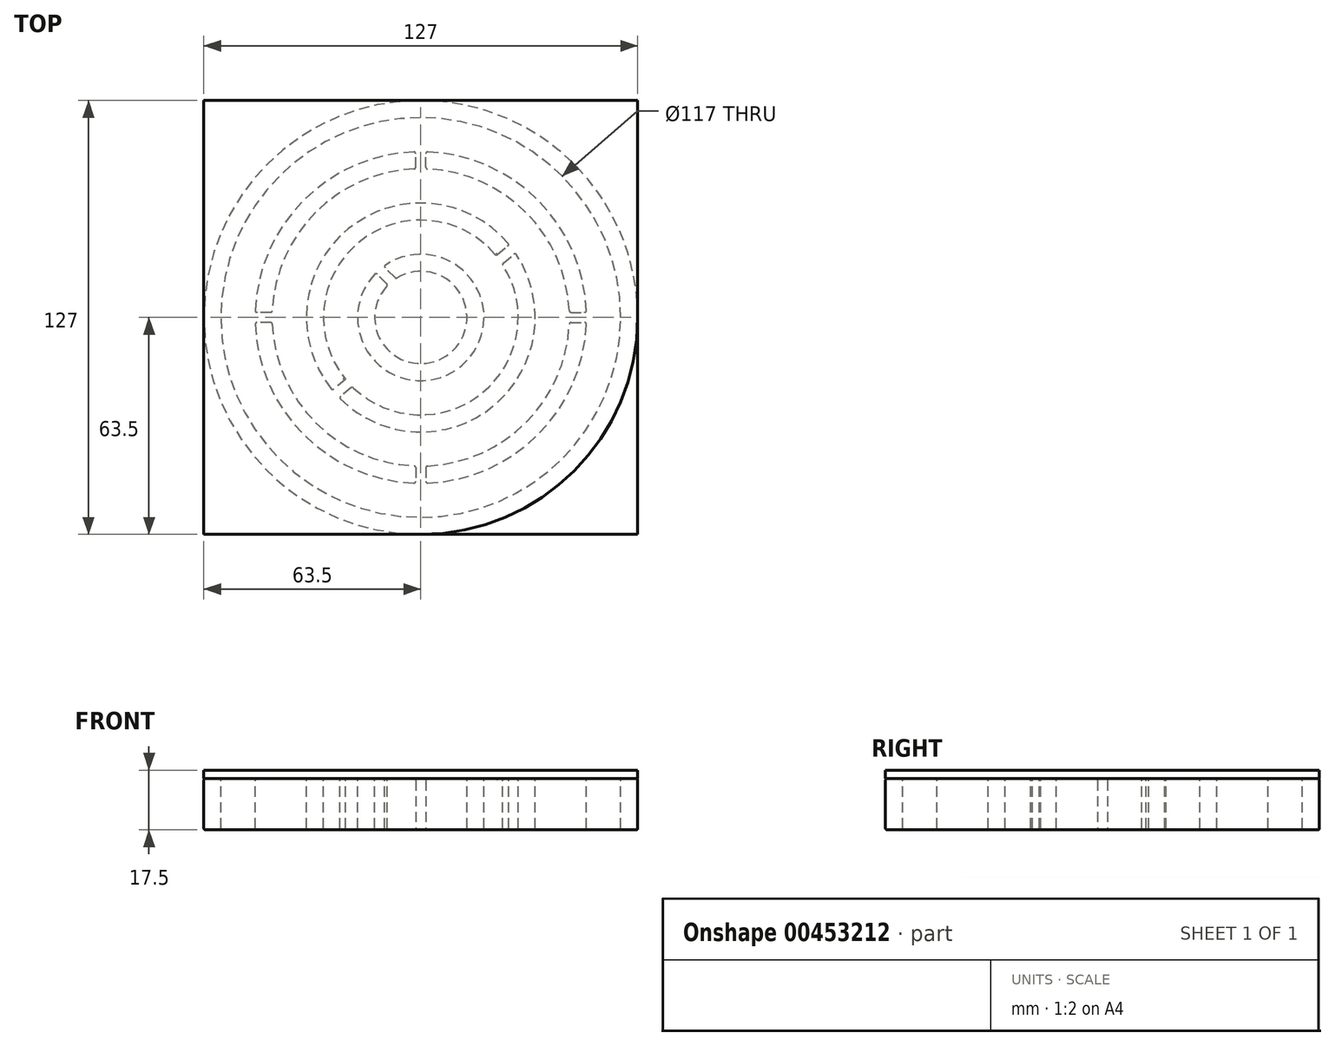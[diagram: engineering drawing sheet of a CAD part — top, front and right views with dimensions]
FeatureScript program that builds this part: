
annotation { "Feature Type Name" : "Feature", "Feature Type Description" : "" }
export const myFeature = defineFeature(function(context is Context, id is Id, definition is map)
    precondition{}
    {
        {
            var Q0;
            Q0=qCreatedBy(makeId("Top.planeOp"),FACE);
            var sketch = newSketch(context, id + "F0", { "sketchPlane" : qUnion([Q0])});
            skCircle(sketch, "E0", {"center": v(0, 0) * mm, "radius": 63.5 * mm});
            skCircle(sketch, "E1", {"center": v(0, 0) * mm, "radius": 58.5 * mm});
            skCircle(sketch, "E2", {"center": v(0, 0) * mm, "radius": 48.5 * mm});
            skCircle(sketch, "E3", {"center": v(0, 0) * mm, "radius": 43.5 * mm});
            skLineSegment(sketch, "E4", {"start": v(0, 0) * mm, "end": v(0, 48.5) * mm});
            skLineSegment(sketch, "E5", {"start": v(0, 0) * mm, "end": v(0, -48.5) * mm});
            skLineSegment(sketch, "E6", {"start": v(0, 0) * mm, "end": v(48.5, 0) * mm});
            skLineSegment(sketch, "E7", {"start": v(0, 0) * mm, "end": v(-48.5, 0) * mm});
            skLineSegment(sketch, "E8.0", {"start": v(1.5, 0) * mm, "end": v(1.5, 48.5) * mm});
            skLineSegment(sketch, "E9.0", {"start": v(-1.5, 0) * mm, "end": v(-1.5, 48.5) * mm});
            skLineSegment(sketch, "E10.0", {"start": v(-1.5, 0) * mm, "end": v(-1.5, -48.5) * mm});
            skLineSegment(sketch, "E11.0", {"start": v(1.5, 0) * mm, "end": v(1.5, -48.5) * mm});
            skLineSegment(sketch, "E12.0", {"start": v(0, -1.5) * mm, "end": v(48.5, -1.5) * mm});
            skLineSegment(sketch, "E13.0", {"start": v(0, 1.5) * mm, "end": v(48.5, 1.5) * mm});
            skLineSegment(sketch, "E14.0", {"start": v(0, 1.5) * mm, "end": v(-48.5, 1.5) * mm});
            skLineSegment(sketch, "E15.0", {"start": v(0, -1.5) * mm, "end": v(-48.5, -1.5) * mm});
            skCircle(sketch, "E16", {"center": v(0, 0) * mm, "radius": 33.5 * mm});
            skCircle(sketch, "E17", {"center": v(0, 0) * mm, "radius": 28.5 * mm});
            skCircle(sketch, "E18", {"center": v(0, 0) * mm, "radius": 18.5 * mm});
            skCircle(sketch, "E19", {"center": v(0, 0) * mm, "radius": 13.5 * mm});
            skLineSegment(sketch, "E20", {"start": v(0, 0) * mm, "end": v(-13.14, 13.02) * mm});
            skLineSegment(sketch, "E21", {"start": v(0, 0) * mm, "end": v(13.14, -13.02) * mm});
            skLineSegment(sketch, "E22.0", {"start": v(2.11, 2.13) * mm, "end": v(-11.03, 15.15) * mm});
            skLineSegment(sketch, "E23.0", {"start": v(2.11, 2.13) * mm, "end": v(15.25, -10.89) * mm});
            skLineSegment(sketch, "E24", {"start": v(0, 0) * mm, "end": v(-25.9, -21.26) * mm});
            skLineSegment(sketch, "E25", {"start": v(0, 0) * mm, "end": v(25.9, 21.26) * mm});
            skLineSegment(sketch, "E26.0", {"start": v(1.9, -2.32) * mm, "end": v(27.8, 18.94) * mm});
            skLineSegment(sketch, "E27.0", {"start": v(1.9, -2.32) * mm, "end": v(-23.99, -23.57) * mm});
            skSolve(sketch);
        }
        {
            var Q0;
            Q0=makeQuery(id+"F0.imprint","IMPRINT",FACE,{"disambiguationData":[TD([[makeQuery(id+"F0.imprint","IMPRINT",EDGE,{"derivedFrom":sQuery(id+"F0.wireOp",EDGE,"E0")}),1.0]])]});
            var Q1;
            {var subQ0=sQuery(id+"F0.wireOp",EDGE,"E15.0");var subQ1=sQuery(id+"F0.wireOp",EDGE,"E2");var subQ2=makeQuery(id+"F0.imprint","INTERSECT",VERTEX,{"derivedFrom":[subQ1,subQ0]});Q1=makeQuery(id+"F0.imprint","IMPRINT",FACE,{"disambiguationData":[TD([[makeQuery(id+"F0.imprint","IMPRINT",EDGE,{"disambiguationData":[TD([[subQ2,-1.0]])],"derivedFrom":subQ1}),1.0]])]});}
            var Q2;
            {var subQ0=sQuery(id+"F0.wireOp",EDGE,"E9.0");var subQ1=sQuery(id+"F0.wireOp",EDGE,"E2");var subQ2=makeQuery(id+"F0.imprint","INTERSECT",VERTEX,{"derivedFrom":[subQ1,subQ0]});Q2=makeQuery(id+"F0.imprint","IMPRINT",FACE,{"disambiguationData":[TD([[makeQuery(id+"F0.imprint","IMPRINT",EDGE,{"disambiguationData":[TD([[subQ2,-1.0]])],"derivedFrom":subQ1}),1.0]])]});}
            var Q3;
            {var subQ0=sQuery(id+"F0.wireOp",EDGE,"E13.0");var subQ1=sQuery(id+"F0.wireOp",EDGE,"E2");var subQ2=makeQuery(id+"F0.imprint","INTERSECT",VERTEX,{"derivedFrom":[subQ1,subQ0]});Q3=makeQuery(id+"F0.imprint","IMPRINT",FACE,{"disambiguationData":[TD([[makeQuery(id+"F0.imprint","IMPRINT",EDGE,{"disambiguationData":[TD([[subQ2,-1.0]])],"derivedFrom":subQ1}),1.0]])]});}
            var Q4;
            {var subQ0=sQuery(id+"F0.wireOp",EDGE,"E11.0");var subQ1=sQuery(id+"F0.wireOp",EDGE,"E2");var subQ2=makeQuery(id+"F0.imprint","INTERSECT",VERTEX,{"derivedFrom":[subQ1,subQ0]});Q4=makeQuery(id+"F0.imprint","IMPRINT",FACE,{"disambiguationData":[TD([[makeQuery(id+"F0.imprint","IMPRINT",EDGE,{"disambiguationData":[TD([[subQ2,-1.0]])],"derivedFrom":subQ1}),1.0]])]});}
            var Q5;
            {var subQ0=sQuery(id+"F0.wireOp",EDGE,"E17");var subQ1=sQuery(id+"F0.wireOp",EDGE,"E15.0");var subQ2=makeQuery(id+"F0.imprint","INTERSECT",VERTEX,{"derivedFrom":[subQ1,subQ0]});Q5=makeQuery(id+"F0.imprint","IMPRINT",FACE,{"disambiguationData":[TD([[makeQuery(id+"F0.imprint","IMPRINT",EDGE,{"disambiguationData":[TD([[subQ2,-1.0]])],"derivedFrom":subQ1}),1.0]])]});}
            var Q6;
            {var subQ0=sQuery(id+"F0.wireOp",EDGE,"E17");var subQ1=sQuery(id+"F0.wireOp",EDGE,"E7");var subQ2=makeQuery(id+"F0.imprint","INTERSECT",VERTEX,{"derivedFrom":[subQ1,subQ0]});Q6=makeQuery(id+"F0.imprint","IMPRINT",FACE,{"disambiguationData":[TD([[makeQuery(id+"F0.imprint","IMPRINT",EDGE,{"disambiguationData":[TD([[subQ2,-1.0]])],"derivedFrom":subQ1}),1.0]])]});}
            var Q7;
            {var subQ0=sQuery(id+"F0.wireOp",EDGE,"E17");var subQ1=sQuery(id+"F0.wireOp",EDGE,"E7");var subQ2=makeQuery(id+"F0.imprint","INTERSECT",VERTEX,{"derivedFrom":[subQ1,subQ0]});Q7=makeQuery(id+"F0.imprint","IMPRINT",FACE,{"disambiguationData":[TD([[makeQuery(id+"F0.imprint","IMPRINT",EDGE,{"disambiguationData":[TD([[subQ2,-1.0]])],"derivedFrom":subQ1}),-1.0]])]});}
            var Q8;
            {var subQ0=sQuery(id+"F0.wireOp",EDGE,"E17");var subQ1=sQuery(id+"F0.wireOp",EDGE,"E9.0");var subQ2=makeQuery(id+"F0.imprint","INTERSECT",VERTEX,{"derivedFrom":[subQ1,subQ0]});Q8=makeQuery(id+"F0.imprint","IMPRINT",FACE,{"disambiguationData":[TD([[makeQuery(id+"F0.imprint","IMPRINT",EDGE,{"disambiguationData":[TD([[subQ2,-1.0]])],"derivedFrom":subQ1}),1.0]])]});}
            var Q9;
            {var subQ0=sQuery(id+"F0.wireOp",EDGE,"E17");var subQ1=sQuery(id+"F0.wireOp",EDGE,"E4");var subQ2=makeQuery(id+"F0.imprint","INTERSECT",VERTEX,{"derivedFrom":[subQ1,subQ0]});Q9=makeQuery(id+"F0.imprint","IMPRINT",FACE,{"disambiguationData":[TD([[makeQuery(id+"F0.imprint","IMPRINT",EDGE,{"disambiguationData":[TD([[subQ2,-1.0]])],"derivedFrom":subQ1}),1.0]])]});}
            var Q10;
            {var subQ0=sQuery(id+"F0.wireOp",EDGE,"E17");var subQ1=sQuery(id+"F0.wireOp",EDGE,"E4");var subQ2=makeQuery(id+"F0.imprint","INTERSECT",VERTEX,{"derivedFrom":[subQ1,subQ0]});Q10=makeQuery(id+"F0.imprint","IMPRINT",FACE,{"disambiguationData":[TD([[makeQuery(id+"F0.imprint","IMPRINT",EDGE,{"disambiguationData":[TD([[subQ2,-1.0]])],"derivedFrom":subQ1}),-1.0]])]});}
            var Q11;
            {var subQ0=sQuery(id+"F0.wireOp",EDGE,"E17");var subQ1=sQuery(id+"F0.wireOp",EDGE,"E8.0");var subQ2=makeQuery(id+"F0.imprint","INTERSECT",VERTEX,{"derivedFrom":[subQ1,subQ0]});Q11=makeQuery(id+"F0.imprint","IMPRINT",FACE,{"disambiguationData":[TD([[makeQuery(id+"F0.imprint","IMPRINT",EDGE,{"disambiguationData":[TD([[subQ2,-1.0]])],"derivedFrom":subQ1}),-1.0]])]});}
            var Q12;
            {var subQ0=sQuery(id+"F0.wireOp",EDGE,"E17");var subQ1=sQuery(id+"F0.wireOp",EDGE,"E13.0");var subQ2=makeQuery(id+"F0.imprint","INTERSECT",VERTEX,{"derivedFrom":[subQ1,subQ0]});Q12=makeQuery(id+"F0.imprint","IMPRINT",FACE,{"disambiguationData":[TD([[makeQuery(id+"F0.imprint","IMPRINT",EDGE,{"disambiguationData":[TD([[subQ2,-1.0]])],"derivedFrom":subQ1}),1.0]])]});}
            var Q13;
            {var subQ0=sQuery(id+"F0.wireOp",EDGE,"E17");var subQ1=sQuery(id+"F0.wireOp",EDGE,"E6");var subQ2=makeQuery(id+"F0.imprint","INTERSECT",VERTEX,{"derivedFrom":[subQ1,subQ0]});Q13=makeQuery(id+"F0.imprint","IMPRINT",FACE,{"disambiguationData":[TD([[makeQuery(id+"F0.imprint","IMPRINT",EDGE,{"disambiguationData":[TD([[subQ2,-1.0]])],"derivedFrom":subQ1}),1.0]])]});}
            var Q14;
            {var subQ0=sQuery(id+"F0.wireOp",EDGE,"E17");var subQ1=sQuery(id+"F0.wireOp",EDGE,"E6");var subQ2=makeQuery(id+"F0.imprint","INTERSECT",VERTEX,{"derivedFrom":[subQ1,subQ0]});Q14=makeQuery(id+"F0.imprint","IMPRINT",FACE,{"disambiguationData":[TD([[makeQuery(id+"F0.imprint","IMPRINT",EDGE,{"disambiguationData":[TD([[subQ2,-1.0]])],"derivedFrom":subQ1}),-1.0]])]});}
            var Q15;
            {var subQ0=sQuery(id+"F0.wireOp",EDGE,"E17");var subQ1=sQuery(id+"F0.wireOp",EDGE,"E11.0");var subQ2=makeQuery(id+"F0.imprint","INTERSECT",VERTEX,{"derivedFrom":[subQ1,subQ0]});Q15=makeQuery(id+"F0.imprint","IMPRINT",FACE,{"disambiguationData":[TD([[makeQuery(id+"F0.imprint","IMPRINT",EDGE,{"disambiguationData":[TD([[subQ2,-1.0]])],"derivedFrom":subQ1}),1.0]])]});}
            var Q16;
            {var subQ0=sQuery(id+"F0.wireOp",EDGE,"E17");var subQ1=sQuery(id+"F0.wireOp",EDGE,"E5");var subQ2=makeQuery(id+"F0.imprint","INTERSECT",VERTEX,{"derivedFrom":[subQ1,subQ0]});Q16=makeQuery(id+"F0.imprint","IMPRINT",FACE,{"disambiguationData":[TD([[makeQuery(id+"F0.imprint","IMPRINT",EDGE,{"disambiguationData":[TD([[subQ2,-1.0]])],"derivedFrom":subQ1}),1.0]])]});}
            var Q17;
            {var subQ0=sQuery(id+"F0.wireOp",EDGE,"E17");var subQ1=sQuery(id+"F0.wireOp",EDGE,"E5");var subQ2=makeQuery(id+"F0.imprint","INTERSECT",VERTEX,{"derivedFrom":[subQ1,subQ0]});Q17=makeQuery(id+"F0.imprint","IMPRINT",FACE,{"disambiguationData":[TD([[makeQuery(id+"F0.imprint","IMPRINT",EDGE,{"disambiguationData":[TD([[subQ2,-1.0]])],"derivedFrom":subQ1}),-1.0]])]});}
            var Q18;
            {var subQ0=sQuery(id+"F0.wireOp",EDGE,"E17");var subQ1=sQuery(id+"F0.wireOp",EDGE,"E10.0");var subQ2=makeQuery(id+"F0.imprint","INTERSECT",VERTEX,{"derivedFrom":[subQ1,subQ0]});Q18=makeQuery(id+"F0.imprint","IMPRINT",FACE,{"disambiguationData":[TD([[makeQuery(id+"F0.imprint","IMPRINT",EDGE,{"disambiguationData":[TD([[subQ2,-1.0]])],"derivedFrom":subQ1}),-1.0]])]});}
            var Q19;
            {var subQ0=sQuery(id+"F0.wireOp",EDGE,"E19");var subQ1=sQuery(id+"F0.wireOp",EDGE,"E15.0");var subQ2=makeQuery(id+"F0.imprint","INTERSECT",VERTEX,{"derivedFrom":[subQ1,subQ0]});Q19=makeQuery(id+"F0.imprint","IMPRINT",FACE,{"disambiguationData":[TD([[makeQuery(id+"F0.imprint","IMPRINT",EDGE,{"disambiguationData":[TD([[subQ2,-1.0]])],"derivedFrom":subQ1}),1.0]])]});}
            var Q20;
            {var subQ0=sQuery(id+"F0.wireOp",EDGE,"E24");var subQ1=sQuery(id+"F0.wireOp",EDGE,"E18");var subQ2=makeQuery(id+"F0.imprint","INTERSECT",VERTEX,{"derivedFrom":[subQ1,subQ0]});Q20=makeQuery(id+"F0.imprint","IMPRINT",FACE,{"disambiguationData":[TD([[makeQuery(id+"F0.imprint","IMPRINT",EDGE,{"disambiguationData":[TD([[subQ2,-1.0]])],"derivedFrom":subQ1}),1.0]])]});}
            var Q21;
            {var subQ0=sQuery(id+"F0.wireOp",EDGE,"E19");var subQ1=sQuery(id+"F0.wireOp",EDGE,"E10.0");var subQ2=makeQuery(id+"F0.imprint","INTERSECT",VERTEX,{"derivedFrom":[subQ1,subQ0]});Q21=makeQuery(id+"F0.imprint","IMPRINT",FACE,{"disambiguationData":[TD([[makeQuery(id+"F0.imprint","IMPRINT",EDGE,{"disambiguationData":[TD([[subQ2,-1.0]])],"derivedFrom":subQ1}),-1.0]])]});}
            var Q22;
            {var subQ0=sQuery(id+"F0.wireOp",EDGE,"E19");var subQ1=sQuery(id+"F0.wireOp",EDGE,"E5");var subQ2=makeQuery(id+"F0.imprint","INTERSECT",VERTEX,{"derivedFrom":[subQ1,subQ0]});Q22=makeQuery(id+"F0.imprint","IMPRINT",FACE,{"disambiguationData":[TD([[makeQuery(id+"F0.imprint","IMPRINT",EDGE,{"disambiguationData":[TD([[subQ2,-1.0]])],"derivedFrom":subQ1}),-1.0]])]});}
            var Q23;
            {var subQ0=sQuery(id+"F0.wireOp",EDGE,"E19");var subQ1=sQuery(id+"F0.wireOp",EDGE,"E5");var subQ2=makeQuery(id+"F0.imprint","INTERSECT",VERTEX,{"derivedFrom":[subQ1,subQ0]});Q23=makeQuery(id+"F0.imprint","IMPRINT",FACE,{"disambiguationData":[TD([[makeQuery(id+"F0.imprint","IMPRINT",EDGE,{"disambiguationData":[TD([[subQ2,-1.0]])],"derivedFrom":subQ1}),1.0]])]});}
            var Q24;
            {var subQ0=sQuery(id+"F0.wireOp",EDGE,"E19");var subQ1=sQuery(id+"F0.wireOp",EDGE,"E11.0");var subQ2=makeQuery(id+"F0.imprint","INTERSECT",VERTEX,{"derivedFrom":[subQ1,subQ0]});Q24=makeQuery(id+"F0.imprint","IMPRINT",FACE,{"disambiguationData":[TD([[makeQuery(id+"F0.imprint","IMPRINT",EDGE,{"disambiguationData":[TD([[subQ2,-1.0]])],"derivedFrom":subQ1}),1.0]])]});}
            var Q25;
            {var subQ0=sQuery(id+"F0.wireOp",EDGE,"E19");var subQ1=sQuery(id+"F0.wireOp",EDGE,"E12.0");var subQ2=makeQuery(id+"F0.imprint","INTERSECT",VERTEX,{"derivedFrom":[subQ1,subQ0]});Q25=makeQuery(id+"F0.imprint","IMPRINT",FACE,{"disambiguationData":[TD([[makeQuery(id+"F0.imprint","IMPRINT",EDGE,{"disambiguationData":[TD([[subQ2,-1.0]])],"derivedFrom":subQ1}),-1.0]])]});}
            var Q26;
            {var subQ0=sQuery(id+"F0.wireOp",EDGE,"E19");var subQ1=sQuery(id+"F0.wireOp",EDGE,"E6");var subQ2=makeQuery(id+"F0.imprint","INTERSECT",VERTEX,{"derivedFrom":[subQ1,subQ0]});Q26=makeQuery(id+"F0.imprint","IMPRINT",FACE,{"disambiguationData":[TD([[makeQuery(id+"F0.imprint","IMPRINT",EDGE,{"disambiguationData":[TD([[subQ2,-1.0]])],"derivedFrom":subQ1}),-1.0]])]});}
            var Q27;
            {var subQ0=sQuery(id+"F0.wireOp",EDGE,"E19");var subQ1=sQuery(id+"F0.wireOp",EDGE,"E6");var subQ2=makeQuery(id+"F0.imprint","INTERSECT",VERTEX,{"derivedFrom":[subQ1,subQ0]});Q27=makeQuery(id+"F0.imprint","IMPRINT",FACE,{"disambiguationData":[TD([[makeQuery(id+"F0.imprint","IMPRINT",EDGE,{"disambiguationData":[TD([[subQ2,-1.0]])],"derivedFrom":subQ1}),1.0]])]});}
            var Q28;
            {var subQ0=sQuery(id+"F0.wireOp",EDGE,"E19");var subQ1=sQuery(id+"F0.wireOp",EDGE,"E7");var subQ2=makeQuery(id+"F0.imprint","INTERSECT",VERTEX,{"derivedFrom":[subQ1,subQ0]});Q28=makeQuery(id+"F0.imprint","IMPRINT",FACE,{"disambiguationData":[TD([[makeQuery(id+"F0.imprint","IMPRINT",EDGE,{"disambiguationData":[TD([[subQ2,-1.0]])],"derivedFrom":subQ1}),1.0]])]});}
            var Q29;
            {var subQ0=sQuery(id+"F0.wireOp",EDGE,"E19");var subQ1=sQuery(id+"F0.wireOp",EDGE,"E7");var subQ2=makeQuery(id+"F0.imprint","INTERSECT",VERTEX,{"derivedFrom":[subQ1,subQ0]});Q29=makeQuery(id+"F0.imprint","IMPRINT",FACE,{"disambiguationData":[TD([[makeQuery(id+"F0.imprint","IMPRINT",EDGE,{"disambiguationData":[TD([[subQ2,-1.0]])],"derivedFrom":subQ1}),-1.0]])]});}
            var Q30;
            {var subQ0=sQuery(id+"F0.wireOp",EDGE,"E19");var subQ1=sQuery(id+"F0.wireOp",EDGE,"E14.0");var subQ2=makeQuery(id+"F0.imprint","INTERSECT",VERTEX,{"derivedFrom":[subQ1,subQ0]});Q30=makeQuery(id+"F0.imprint","IMPRINT",FACE,{"disambiguationData":[TD([[makeQuery(id+"F0.imprint","IMPRINT",EDGE,{"disambiguationData":[TD([[subQ2,-1.0]])],"derivedFrom":subQ1}),-1.0]])]});}
            var Q31;
            {var subQ0=sQuery(id+"F0.wireOp",EDGE,"E19");var subQ1=sQuery(id+"F0.wireOp",EDGE,"E9.0");var subQ2=makeQuery(id+"F0.imprint","INTERSECT",VERTEX,{"derivedFrom":[subQ1,subQ0]});Q31=makeQuery(id+"F0.imprint","IMPRINT",FACE,{"disambiguationData":[TD([[makeQuery(id+"F0.imprint","IMPRINT",EDGE,{"disambiguationData":[TD([[subQ2,-1.0]])],"derivedFrom":subQ1}),1.0]])]});}
            var Q32;
            {var subQ0=sQuery(id+"F0.wireOp",EDGE,"E19");var subQ1=sQuery(id+"F0.wireOp",EDGE,"E4");var subQ2=makeQuery(id+"F0.imprint","INTERSECT",VERTEX,{"derivedFrom":[subQ1,subQ0]});Q32=makeQuery(id+"F0.imprint","IMPRINT",FACE,{"disambiguationData":[TD([[makeQuery(id+"F0.imprint","IMPRINT",EDGE,{"disambiguationData":[TD([[subQ2,-1.0]])],"derivedFrom":subQ1}),1.0]])]});}
            var Q33;
            {var subQ0=sQuery(id+"F0.wireOp",EDGE,"E19");var subQ1=sQuery(id+"F0.wireOp",EDGE,"E4");var subQ2=makeQuery(id+"F0.imprint","INTERSECT",VERTEX,{"derivedFrom":[subQ1,subQ0]});Q33=makeQuery(id+"F0.imprint","IMPRINT",FACE,{"disambiguationData":[TD([[makeQuery(id+"F0.imprint","IMPRINT",EDGE,{"disambiguationData":[TD([[subQ2,-1.0]])],"derivedFrom":subQ1}),-1.0]])]});}
            var Q34;
            {var subQ0=sQuery(id+"F0.wireOp",EDGE,"E19");var subQ1=sQuery(id+"F0.wireOp",EDGE,"E8.0");var subQ2=makeQuery(id+"F0.imprint","INTERSECT",VERTEX,{"derivedFrom":[subQ1,subQ0]});Q34=makeQuery(id+"F0.imprint","IMPRINT",FACE,{"disambiguationData":[TD([[makeQuery(id+"F0.imprint","IMPRINT",EDGE,{"disambiguationData":[TD([[subQ2,-1.0]])],"derivedFrom":subQ1}),-1.0]])]});}
            var Q35;
            {var subQ0=sQuery(id+"F0.wireOp",EDGE,"E19");var subQ1=sQuery(id+"F0.wireOp",EDGE,"E13.0");var subQ2=makeQuery(id+"F0.imprint","INTERSECT",VERTEX,{"derivedFrom":[subQ1,subQ0]});Q35=makeQuery(id+"F0.imprint","IMPRINT",FACE,{"disambiguationData":[TD([[makeQuery(id+"F0.imprint","IMPRINT",EDGE,{"disambiguationData":[TD([[subQ2,-1.0]])],"derivedFrom":subQ1}),1.0]])]});}
            var Q36;
            {var subQ0=sQuery(id+"F0.wireOp",EDGE,"E26.0");var subQ1=sQuery(id+"F0.wireOp",EDGE,"E18");var subQ2=makeQuery(id+"F0.imprint","INTERSECT",VERTEX,{"derivedFrom":[subQ1,subQ0]});Q36=makeQuery(id+"F0.imprint","IMPRINT",FACE,{"disambiguationData":[TD([[makeQuery(id+"F0.imprint","IMPRINT",EDGE,{"disambiguationData":[TD([[subQ2,-1.0]])],"derivedFrom":subQ1}),1.0]])]});}
            var Q37;
            {var subQ0=sQuery(id+"F0.wireOp",EDGE,"E21");var subQ1=sQuery(id+"F0.wireOp",EDGE,"E18");var subQ2=makeQuery(id+"F0.imprint","INTERSECT",VERTEX,{"derivedFrom":[subQ1,subQ0]});Q37=makeQuery(id+"F0.imprint","IMPRINT",FACE,{"disambiguationData":[TD([[makeQuery(id+"F0.imprint","IMPRINT",EDGE,{"disambiguationData":[TD([[subQ2,-1.0]])],"derivedFrom":subQ1}),1.0]])]});}
            extrude(context, id + "F1", {"entities" : qUnion([Q0, Q1, Q2, Q3, Q4, Q5, Q6, Q7, Q8, Q9, Q10, Q11, Q12, Q13, Q14, Q15, Q16, Q17, Q18, Q19, Q20, Q21, Q22, Q23, Q24, Q25, Q26, Q27, Q28, Q29, Q30, Q31, Q32, Q33, Q34, Q35, Q36, Q37]), "oppositeDirection" : true, "depth" : 15 * mm});
        }
        {
            var Q0;
            Q0=makeQuery(id+"F1.opExtrude","SWEPT_EDGE",EDGE,{"disambiguationData":[OSD([sQuery(id+"F0.wireOp",EDGE,"E2"),sQuery(id+"F0.wireOp",EDGE,"E14.0")])]});
            var Q1;
            Q1=makeQuery(id+"F1.opExtrude","SWEPT_EDGE",EDGE,{"disambiguationData":[OSD([sQuery(id+"F0.wireOp",EDGE,"E2"),sQuery(id+"F0.wireOp",EDGE,"E15.0")])]});
            var Q2;
            Q2=makeQuery(id+"F1.opExtrude","SWEPT_EDGE",EDGE,{"disambiguationData":[OSD([sQuery(id+"F0.wireOp",EDGE,"E2"),sQuery(id+"F0.wireOp",EDGE,"E8.0")])]});
            var Q3;
            Q3=makeQuery(id+"F1.opExtrude","SWEPT_EDGE",EDGE,{"disambiguationData":[OSD([sQuery(id+"F0.wireOp",EDGE,"E2"),sQuery(id+"F0.wireOp",EDGE,"E9.0")])]});
            var Q4;
            Q4=makeQuery(id+"F1.opExtrude","SWEPT_EDGE",EDGE,{"disambiguationData":[OSD([sQuery(id+"F0.wireOp",EDGE,"E3"),sQuery(id+"F0.wireOp",EDGE,"E15.0")])]});
            var Q5;
            Q5=makeQuery(id+"F1.opExtrude","SWEPT_EDGE",EDGE,{"disambiguationData":[OSD([sQuery(id+"F0.wireOp",EDGE,"E3"),sQuery(id+"F0.wireOp",EDGE,"E14.0")])]});
            var Q6;
            Q6=makeQuery(id+"F1.opExtrude","SWEPT_EDGE",EDGE,{"disambiguationData":[OSD([sQuery(id+"F0.wireOp",EDGE,"E3"),sQuery(id+"F0.wireOp",EDGE,"E9.0")])]});
            var Q7;
            Q7=makeQuery(id+"F1.opExtrude","SWEPT_EDGE",EDGE,{"disambiguationData":[OSD([sQuery(id+"F0.wireOp",EDGE,"E3"),sQuery(id+"F0.wireOp",EDGE,"E8.0")])]});
            var Q8;
            Q8=makeQuery(id+"F1.opExtrude","SWEPT_EDGE",EDGE,{"disambiguationData":[OSD([sQuery(id+"F0.wireOp",EDGE,"E2"),sQuery(id+"F0.wireOp",EDGE,"E10.0")])]});
            var Q9;
            Q9=makeQuery(id+"F1.opExtrude","SWEPT_EDGE",EDGE,{"disambiguationData":[OSD([sQuery(id+"F0.wireOp",EDGE,"E3"),sQuery(id+"F0.wireOp",EDGE,"E10.0")])]});
            var Q10;
            Q10=makeQuery(id+"F1.opExtrude","SWEPT_EDGE",EDGE,{"disambiguationData":[OSD([sQuery(id+"F0.wireOp",EDGE,"E2"),sQuery(id+"F0.wireOp",EDGE,"E11.0")])]});
            var Q11;
            Q11=makeQuery(id+"F1.opExtrude","SWEPT_EDGE",EDGE,{"disambiguationData":[OSD([sQuery(id+"F0.wireOp",EDGE,"E3"),sQuery(id+"F0.wireOp",EDGE,"E11.0")])]});
            var Q12;
            Q12=makeQuery(id+"F1.opExtrude","SWEPT_EDGE",EDGE,{"disambiguationData":[OSD([sQuery(id+"F0.wireOp",EDGE,"E3"),sQuery(id+"F0.wireOp",EDGE,"E13.0")])]});
            var Q13;
            Q13=makeQuery(id+"F1.opExtrude","SWEPT_EDGE",EDGE,{"disambiguationData":[OSD([sQuery(id+"F0.wireOp",EDGE,"E2"),sQuery(id+"F0.wireOp",EDGE,"E13.0")])]});
            var Q14;
            Q14=makeQuery(id+"F1.opExtrude","SWEPT_EDGE",EDGE,{"disambiguationData":[OSD([sQuery(id+"F0.wireOp",EDGE,"E3"),sQuery(id+"F0.wireOp",EDGE,"E12.0")])]});
            var Q15;
            Q15=makeQuery(id+"F1.opExtrude","SWEPT_EDGE",EDGE,{"disambiguationData":[OSD([sQuery(id+"F0.wireOp",EDGE,"E2"),sQuery(id+"F0.wireOp",EDGE,"E12.0")])]});
            var Q16;
            Q16=makeQuery(id+"F1.opExtrude","SWEPT_EDGE",EDGE,{"disambiguationData":[OSD([sQuery(id+"F0.wireOp",EDGE,"E16"),sQuery(id+"F0.wireOp",EDGE,"E25")])]});
            var Q17;
            Q17=makeQuery(id+"F1.opExtrude","SWEPT_EDGE",EDGE,{"disambiguationData":[OSD([sQuery(id+"F0.wireOp",EDGE,"E16"),sQuery(id+"F0.wireOp",EDGE,"E26.0")])]});
            var Q18;
            Q18=makeQuery(id+"F1.opExtrude","SWEPT_EDGE",EDGE,{"disambiguationData":[OSD([sQuery(id+"F0.wireOp",EDGE,"E17"),sQuery(id+"F0.wireOp",EDGE,"E25")])]});
            var Q19;
            Q19=makeQuery(id+"F1.opExtrude","SWEPT_EDGE",EDGE,{"disambiguationData":[OSD([sQuery(id+"F0.wireOp",EDGE,"E17"),sQuery(id+"F0.wireOp",EDGE,"E26.0")])]});
            var Q20;
            Q20=makeQuery(id+"F1.opExtrude","SWEPT_EDGE",EDGE,{"disambiguationData":[OSD([sQuery(id+"F0.wireOp",EDGE,"E16"),sQuery(id+"F0.wireOp",EDGE,"E24")])]});
            var Q21;
            Q21=makeQuery(id+"F1.opExtrude","SWEPT_EDGE",EDGE,{"disambiguationData":[OSD([sQuery(id+"F0.wireOp",EDGE,"E19"),sQuery(id+"F0.wireOp",EDGE,"E22.0")])]});
            var Q22;
            Q22=makeQuery(id+"F1.opExtrude","SWEPT_EDGE",EDGE,{"disambiguationData":[OSD([sQuery(id+"F0.wireOp",EDGE,"E19"),sQuery(id+"F0.wireOp",EDGE,"E20")])]});
            var Q23;
            Q23=makeQuery(id+"F1.opExtrude","SWEPT_EDGE",EDGE,{"disambiguationData":[OSD([sQuery(id+"F0.wireOp",EDGE,"E18"),sQuery(id+"F0.wireOp",EDGE,"E22.0")])]});
            var Q24;
            Q24=makeQuery(id+"F1.opExtrude","SWEPT_EDGE",EDGE,{"disambiguationData":[OSD([sQuery(id+"F0.wireOp",EDGE,"E18"),sQuery(id+"F0.wireOp",EDGE,"E20")])]});
            var Q25;
            Q25=makeQuery(id+"F1.opExtrude","SWEPT_EDGE",EDGE,{"disambiguationData":[OSD([sQuery(id+"F0.wireOp",EDGE,"E16"),sQuery(id+"F0.wireOp",EDGE,"E27.0")])]});
            var Q26;
            Q26=makeQuery(id+"F1.opExtrude","SWEPT_EDGE",EDGE,{"disambiguationData":[OSD([sQuery(id+"F0.wireOp",EDGE,"E17"),sQuery(id+"F0.wireOp",EDGE,"E27.0")])]});
            fillet(context, id + "F2", {"entities" : qUnion([Q0, Q1, Q2, Q3, Q4, Q5, Q6, Q7, Q8, Q9, Q10, Q11, Q12, Q13, Q14, Q15, Q16, Q17, Q18, Q19, Q20, Q21, Q22, Q23, Q24, Q25, Q26]), "radius" : 0.5 * mm, "tangentPropagation" : true, "allowEdgeOverflow" : false});
        }
        {
            var Q0;
            Q0=makeQuery(id+"F1.opExtrude","CAP_EDGE",EDGE,{"disambiguationData":[OSD([sQuery(id+"F0.wireOp",EDGE,"E0")])],"isStart":true});
            var Q1;
            Q1=makeQuery(id+"F1.opExtrude","CAP_EDGE",EDGE,{"disambiguationData":[OSD([sQuery(id+"F0.wireOp",EDGE,"E1")])],"isStart":true});
            var Q2;
            {var subQ0=sQuery(id+"F0.wireOp",EDGE,"E2");Q2=makeQuery(id+"F1.opExtrude","CAP_EDGE",EDGE,{"disambiguationData":[OSD([subQ0]),TDD([makeQuery(id+"F0.imprint","IMPRINT",EDGE,{"disambiguationData":[TD([[makeQuery(id+"F0.imprint","INTERSECT",VERTEX,{"derivedFrom":[subQ0,sQuery(id+"F0.wireOp",EDGE,"E15.0")]}),-1.0]])],"derivedFrom":subQ0})])],"isStart":true});}
            var Q3;
            {var subQ0=sQuery(id+"F0.wireOp",EDGE,"E3");Q3=makeQuery(id+"F1.opExtrude","CAP_EDGE",EDGE,{"disambiguationData":[OSD([subQ0]),TDD([makeQuery(id+"F0.imprint","IMPRINT",EDGE,{"disambiguationData":[TD([[makeQuery(id+"F0.imprint","INTERSECT",VERTEX,{"derivedFrom":[subQ0,sQuery(id+"F0.wireOp",EDGE,"E15.0")]}),-1.0]])],"derivedFrom":subQ0})])],"isStart":true});}
            var Q4;
            {var subQ0=sQuery(id+"F0.wireOp",EDGE,"E2");Q4=makeQuery(id+"F1.opExtrude","CAP_EDGE",EDGE,{"disambiguationData":[OSD([subQ0]),TDD([makeQuery(id+"F0.imprint","IMPRINT",EDGE,{"disambiguationData":[TD([[makeQuery(id+"F0.imprint","INTERSECT",VERTEX,{"derivedFrom":[subQ0,sQuery(id+"F0.wireOp",EDGE,"E11.0")]}),-1.0]])],"derivedFrom":subQ0})])],"isStart":true});}
            var Q5;
            {var subQ0=sQuery(id+"F0.wireOp",EDGE,"E3");Q5=makeQuery(id+"F1.opExtrude","CAP_EDGE",EDGE,{"disambiguationData":[OSD([subQ0]),TDD([makeQuery(id+"F0.imprint","IMPRINT",EDGE,{"disambiguationData":[TD([[makeQuery(id+"F0.imprint","INTERSECT",VERTEX,{"derivedFrom":[subQ0,sQuery(id+"F0.wireOp",EDGE,"E11.0")]}),-1.0]])],"derivedFrom":subQ0})])],"isStart":true});}
            var Q6;
            {var subQ0=sQuery(id+"F0.wireOp",EDGE,"E16");var subQ1=makeQuery(id+"F0.imprint","INTERSECT",VERTEX,{"derivedFrom":[sQuery(id+"F0.wireOp",EDGE,"E6"),subQ0]});var subQ3=makeQuery(id+"F0.imprint","INTERSECT",VERTEX,{"derivedFrom":[sQuery(id+"F0.wireOp",EDGE,"E11.0"),subQ0]});var subQ4=makeQuery(id+"F0.imprint","INTERSECT",VERTEX,{"derivedFrom":[sQuery(id+"F0.wireOp",EDGE,"E5"),subQ0]});Q6=makeQuery(id+"F1.opExtrude","CAP_EDGE",EDGE,{"disambiguationData":[OSD([subQ0]),TDD([makeQuery(id+"F0.imprint","IMPRINT",EDGE,{"disambiguationData":[TD([[subQ1,-1.0]])],"derivedFrom":subQ0}),makeQuery(id+"F0.imprint","IMPRINT",EDGE,{"disambiguationData":[TD([[makeQuery(id+"F0.imprint","INTERSECT",VERTEX,{"derivedFrom":[subQ0,sQuery(id+"F0.wireOp",EDGE,"E26.0")]}),1.0]])],"derivedFrom":subQ0}),makeQuery(id+"F0.imprint","IMPRINT",EDGE,{"disambiguationData":[TD([[makeQuery(id+"F0.imprint","INTERSECT",VERTEX,{"derivedFrom":[subQ0,sQuery(id+"F0.wireOp",EDGE,"E27.0")]}),-1.0]])],"derivedFrom":subQ0}),makeQuery(id+"F0.imprint","IMPRINT",EDGE,{"disambiguationData":[TD([[subQ4,1.0]])],"derivedFrom":subQ0}),makeQuery(id+"F0.imprint","IMPRINT",EDGE,{"disambiguationData":[TD([[subQ4,-1.0]])],"derivedFrom":subQ0}),makeQuery(id+"F0.imprint","IMPRINT",EDGE,{"disambiguationData":[TD([[subQ3,-1.0]])],"derivedFrom":subQ0}),makeQuery(id+"F0.imprint","IMPRINT",EDGE,{"disambiguationData":[TD([[subQ1,1.0]])],"derivedFrom":subQ0})])],"isStart":true});}
            var Q7;
            {var subQ0=sQuery(id+"F0.wireOp",EDGE,"E17");var subQ1=makeQuery(id+"F0.imprint","INTERSECT",VERTEX,{"derivedFrom":[sQuery(id+"F0.wireOp",EDGE,"E6"),subQ0]});var subQ3=makeQuery(id+"F0.imprint","INTERSECT",VERTEX,{"derivedFrom":[sQuery(id+"F0.wireOp",EDGE,"E11.0"),subQ0]});var subQ4=makeQuery(id+"F0.imprint","INTERSECT",VERTEX,{"derivedFrom":[sQuery(id+"F0.wireOp",EDGE,"E5"),subQ0]});var subQ5=makeQuery(id+"F0.imprint","INTERSECT",VERTEX,{"derivedFrom":[sQuery(id+"F0.wireOp",EDGE,"E10.0"),subQ0]});var subQ6=makeQuery(id+"F0.imprint","INTERSECT",VERTEX,{"derivedFrom":[sQuery(id+"F0.wireOp",EDGE,"E13.0"),subQ0]});Q7=makeQuery(id+"F1.opExtrude","CAP_EDGE",EDGE,{"disambiguationData":[OSD([subQ0]),TDD([makeQuery(id+"F0.imprint","IMPRINT",EDGE,{"disambiguationData":[TD([[subQ1,-1.0]])],"derivedFrom":subQ0}),makeQuery(id+"F0.imprint","IMPRINT",EDGE,{"disambiguationData":[TD([[subQ6,-1.0]])],"derivedFrom":subQ0}),makeQuery(id+"F0.imprint","IMPRINT",EDGE,{"disambiguationData":[TD([[subQ5,1.0]])],"derivedFrom":subQ0}),makeQuery(id+"F0.imprint","IMPRINT",EDGE,{"disambiguationData":[TD([[subQ4,1.0]])],"derivedFrom":subQ0}),makeQuery(id+"F0.imprint","IMPRINT",EDGE,{"disambiguationData":[TD([[subQ4,-1.0]])],"derivedFrom":subQ0}),makeQuery(id+"F0.imprint","IMPRINT",EDGE,{"disambiguationData":[TD([[subQ3,-1.0]])],"derivedFrom":subQ0}),makeQuery(id+"F0.imprint","IMPRINT",EDGE,{"disambiguationData":[TD([[subQ1,1.0]])],"derivedFrom":subQ0})])],"isStart":true});}
            var Q8;
            Q8=makeQuery(id+"F1.opExtrude","CAP_EDGE",EDGE,{"disambiguationData":[OSD([sQuery(id+"F0.wireOp",EDGE,"E18")])],"isStart":true});
            var Q9;
            Q9=makeQuery(id+"F1.opExtrude","CAP_EDGE",EDGE,{"disambiguationData":[OSD([sQuery(id+"F0.wireOp",EDGE,"E19")])],"isStart":true});
            var Q10;
            {var subQ0=sQuery(id+"F0.wireOp",EDGE,"E17");var subQ1=makeQuery(id+"F0.imprint","INTERSECT",VERTEX,{"derivedFrom":[sQuery(id+"F0.wireOp",EDGE,"E15.0"),subQ0]});var subQ2=makeQuery(id+"F0.imprint","INTERSECT",VERTEX,{"derivedFrom":[sQuery(id+"F0.wireOp",EDGE,"E7"),subQ0]});var subQ4=makeQuery(id+"F0.imprint","INTERSECT",VERTEX,{"derivedFrom":[sQuery(id+"F0.wireOp",EDGE,"E9.0"),subQ0]});var subQ5=makeQuery(id+"F0.imprint","INTERSECT",VERTEX,{"derivedFrom":[sQuery(id+"F0.wireOp",EDGE,"E4"),subQ0]});var subQ6=makeQuery(id+"F0.imprint","INTERSECT",VERTEX,{"derivedFrom":[sQuery(id+"F0.wireOp",EDGE,"E8.0"),subQ0]});Q10=makeQuery(id+"F1.opExtrude","CAP_EDGE",EDGE,{"disambiguationData":[OSD([subQ0]),TDD([makeQuery(id+"F0.imprint","IMPRINT",EDGE,{"disambiguationData":[TD([[subQ6,1.0]])],"derivedFrom":subQ0}),makeQuery(id+"F0.imprint","IMPRINT",EDGE,{"disambiguationData":[TD([[subQ5,1.0]])],"derivedFrom":subQ0}),makeQuery(id+"F0.imprint","IMPRINT",EDGE,{"disambiguationData":[TD([[subQ5,-1.0]])],"derivedFrom":subQ0}),makeQuery(id+"F0.imprint","IMPRINT",EDGE,{"disambiguationData":[TD([[subQ4,-1.0]])],"derivedFrom":subQ0}),makeQuery(id+"F0.imprint","IMPRINT",EDGE,{"disambiguationData":[TD([[subQ2,1.0]])],"derivedFrom":subQ0}),makeQuery(id+"F0.imprint","IMPRINT",EDGE,{"disambiguationData":[TD([[subQ2,-1.0]])],"derivedFrom":subQ0}),makeQuery(id+"F0.imprint","IMPRINT",EDGE,{"disambiguationData":[TD([[subQ1,-1.0]])],"derivedFrom":subQ0})])],"isStart":true});}
            var Q11;
            {var subQ0=sQuery(id+"F0.wireOp",EDGE,"E16");var subQ2=makeQuery(id+"F0.imprint","INTERSECT",VERTEX,{"derivedFrom":[sQuery(id+"F0.wireOp",EDGE,"E7"),subQ0]});var subQ4=makeQuery(id+"F0.imprint","INTERSECT",VERTEX,{"derivedFrom":[sQuery(id+"F0.wireOp",EDGE,"E9.0"),subQ0]});var subQ5=makeQuery(id+"F0.imprint","INTERSECT",VERTEX,{"derivedFrom":[sQuery(id+"F0.wireOp",EDGE,"E4"),subQ0]});Q11=makeQuery(id+"F1.opExtrude","CAP_EDGE",EDGE,{"disambiguationData":[OSD([subQ0]),TDD([makeQuery(id+"F0.imprint","IMPRINT",EDGE,{"disambiguationData":[TD([[makeQuery(id+"F0.imprint","INTERSECT",VERTEX,{"derivedFrom":[subQ0,sQuery(id+"F0.wireOp",EDGE,"E25")]}),-1.0]])],"derivedFrom":subQ0}),makeQuery(id+"F0.imprint","IMPRINT",EDGE,{"disambiguationData":[TD([[subQ5,1.0]])],"derivedFrom":subQ0}),makeQuery(id+"F0.imprint","IMPRINT",EDGE,{"disambiguationData":[TD([[subQ5,-1.0]])],"derivedFrom":subQ0}),makeQuery(id+"F0.imprint","IMPRINT",EDGE,{"disambiguationData":[TD([[subQ4,-1.0]])],"derivedFrom":subQ0}),makeQuery(id+"F0.imprint","IMPRINT",EDGE,{"disambiguationData":[TD([[subQ2,1.0]])],"derivedFrom":subQ0}),makeQuery(id+"F0.imprint","IMPRINT",EDGE,{"disambiguationData":[TD([[subQ2,-1.0]])],"derivedFrom":subQ0}),makeQuery(id+"F0.imprint","IMPRINT",EDGE,{"disambiguationData":[TD([[makeQuery(id+"F0.imprint","INTERSECT",VERTEX,{"derivedFrom":[subQ0,sQuery(id+"F0.wireOp",EDGE,"E24")]}),1.0]])],"derivedFrom":subQ0})])],"isStart":true});}
            var Q12;
            {var subQ0=sQuery(id+"F0.wireOp",EDGE,"E3");Q12=makeQuery(id+"F1.opExtrude","CAP_EDGE",EDGE,{"disambiguationData":[OSD([subQ0]),TDD([makeQuery(id+"F0.imprint","IMPRINT",EDGE,{"disambiguationData":[TD([[makeQuery(id+"F0.imprint","INTERSECT",VERTEX,{"derivedFrom":[subQ0,sQuery(id+"F0.wireOp",EDGE,"E9.0")]}),-1.0]])],"derivedFrom":subQ0})])],"isStart":true});}
            var Q13;
            {var subQ0=sQuery(id+"F0.wireOp",EDGE,"E2");Q13=makeQuery(id+"F1.opExtrude","CAP_EDGE",EDGE,{"disambiguationData":[OSD([subQ0]),TDD([makeQuery(id+"F0.imprint","IMPRINT",EDGE,{"disambiguationData":[TD([[makeQuery(id+"F0.imprint","INTERSECT",VERTEX,{"derivedFrom":[subQ0,sQuery(id+"F0.wireOp",EDGE,"E9.0")]}),-1.0]])],"derivedFrom":subQ0})])],"isStart":true});}
            var Q14;
            {var subQ0=sQuery(id+"F0.wireOp",EDGE,"E3");Q14=makeQuery(id+"F1.opExtrude","CAP_EDGE",EDGE,{"disambiguationData":[OSD([subQ0]),TDD([makeQuery(id+"F0.imprint","IMPRINT",EDGE,{"disambiguationData":[TD([[makeQuery(id+"F0.imprint","INTERSECT",VERTEX,{"derivedFrom":[subQ0,sQuery(id+"F0.wireOp",EDGE,"E13.0")]}),-1.0]])],"derivedFrom":subQ0})])],"isStart":true});}
            var Q15;
            {var subQ0=sQuery(id+"F0.wireOp",EDGE,"E2");Q15=makeQuery(id+"F1.opExtrude","CAP_EDGE",EDGE,{"disambiguationData":[OSD([subQ0]),TDD([makeQuery(id+"F0.imprint","IMPRINT",EDGE,{"disambiguationData":[TD([[makeQuery(id+"F0.imprint","INTERSECT",VERTEX,{"derivedFrom":[subQ0,sQuery(id+"F0.wireOp",EDGE,"E13.0")]}),-1.0]])],"derivedFrom":subQ0})])],"isStart":true});}
            var Q16;
            Q16=makeQuery(id+"F1.opExtrude","CAP_EDGE",EDGE,{"disambiguationData":[OSD([sQuery(id+"F0.wireOp",EDGE,"E0")])],"isStart":false});
            var Q17;
            Q17=makeQuery(id+"F1.opExtrude","CAP_EDGE",EDGE,{"disambiguationData":[OSD([sQuery(id+"F0.wireOp",EDGE,"E1")])],"isStart":false});
            var Q18;
            {var subQ0=sQuery(id+"F0.wireOp",EDGE,"E2");Q18=makeQuery(id+"F1.opExtrude","CAP_EDGE",EDGE,{"disambiguationData":[OSD([subQ0]),TDD([makeQuery(id+"F0.imprint","IMPRINT",EDGE,{"disambiguationData":[TD([[makeQuery(id+"F0.imprint","INTERSECT",VERTEX,{"derivedFrom":[subQ0,sQuery(id+"F0.wireOp",EDGE,"E9.0")]}),-1.0]])],"derivedFrom":subQ0})])],"isStart":false});}
            var Q19;
            {var subQ0=sQuery(id+"F0.wireOp",EDGE,"E3");Q19=makeQuery(id+"F1.opExtrude","CAP_EDGE",EDGE,{"disambiguationData":[OSD([subQ0]),TDD([makeQuery(id+"F0.imprint","IMPRINT",EDGE,{"disambiguationData":[TD([[makeQuery(id+"F0.imprint","INTERSECT",VERTEX,{"derivedFrom":[subQ0,sQuery(id+"F0.wireOp",EDGE,"E9.0")]}),-1.0]])],"derivedFrom":subQ0})])],"isStart":false});}
            var Q20;
            {var subQ0=sQuery(id+"F0.wireOp",EDGE,"E2");Q20=makeQuery(id+"F1.opExtrude","CAP_EDGE",EDGE,{"disambiguationData":[OSD([subQ0]),TDD([makeQuery(id+"F0.imprint","IMPRINT",EDGE,{"disambiguationData":[TD([[makeQuery(id+"F0.imprint","INTERSECT",VERTEX,{"derivedFrom":[subQ0,sQuery(id+"F0.wireOp",EDGE,"E13.0")]}),-1.0]])],"derivedFrom":subQ0})])],"isStart":false});}
            var Q21;
            {var subQ0=sQuery(id+"F0.wireOp",EDGE,"E3");Q21=makeQuery(id+"F1.opExtrude","CAP_EDGE",EDGE,{"disambiguationData":[OSD([subQ0]),TDD([makeQuery(id+"F0.imprint","IMPRINT",EDGE,{"disambiguationData":[TD([[makeQuery(id+"F0.imprint","INTERSECT",VERTEX,{"derivedFrom":[subQ0,sQuery(id+"F0.wireOp",EDGE,"E13.0")]}),-1.0]])],"derivedFrom":subQ0})])],"isStart":false});}
            var Q22;
            {var subQ0=sQuery(id+"F0.wireOp",EDGE,"E16");var subQ2=makeQuery(id+"F0.imprint","INTERSECT",VERTEX,{"derivedFrom":[sQuery(id+"F0.wireOp",EDGE,"E7"),subQ0]});var subQ4=makeQuery(id+"F0.imprint","INTERSECT",VERTEX,{"derivedFrom":[sQuery(id+"F0.wireOp",EDGE,"E9.0"),subQ0]});var subQ5=makeQuery(id+"F0.imprint","INTERSECT",VERTEX,{"derivedFrom":[sQuery(id+"F0.wireOp",EDGE,"E4"),subQ0]});Q22=makeQuery(id+"F1.opExtrude","CAP_EDGE",EDGE,{"disambiguationData":[OSD([subQ0]),TDD([makeQuery(id+"F0.imprint","IMPRINT",EDGE,{"disambiguationData":[TD([[makeQuery(id+"F0.imprint","INTERSECT",VERTEX,{"derivedFrom":[subQ0,sQuery(id+"F0.wireOp",EDGE,"E25")]}),-1.0]])],"derivedFrom":subQ0}),makeQuery(id+"F0.imprint","IMPRINT",EDGE,{"disambiguationData":[TD([[subQ5,1.0]])],"derivedFrom":subQ0}),makeQuery(id+"F0.imprint","IMPRINT",EDGE,{"disambiguationData":[TD([[subQ5,-1.0]])],"derivedFrom":subQ0}),makeQuery(id+"F0.imprint","IMPRINT",EDGE,{"disambiguationData":[TD([[subQ4,-1.0]])],"derivedFrom":subQ0}),makeQuery(id+"F0.imprint","IMPRINT",EDGE,{"disambiguationData":[TD([[subQ2,1.0]])],"derivedFrom":subQ0}),makeQuery(id+"F0.imprint","IMPRINT",EDGE,{"disambiguationData":[TD([[subQ2,-1.0]])],"derivedFrom":subQ0}),makeQuery(id+"F0.imprint","IMPRINT",EDGE,{"disambiguationData":[TD([[makeQuery(id+"F0.imprint","INTERSECT",VERTEX,{"derivedFrom":[subQ0,sQuery(id+"F0.wireOp",EDGE,"E24")]}),1.0]])],"derivedFrom":subQ0})])],"isStart":false});}
            var Q23;
            {var subQ0=sQuery(id+"F0.wireOp",EDGE,"E17");var subQ1=makeQuery(id+"F0.imprint","INTERSECT",VERTEX,{"derivedFrom":[sQuery(id+"F0.wireOp",EDGE,"E15.0"),subQ0]});var subQ2=makeQuery(id+"F0.imprint","INTERSECT",VERTEX,{"derivedFrom":[sQuery(id+"F0.wireOp",EDGE,"E7"),subQ0]});var subQ4=makeQuery(id+"F0.imprint","INTERSECT",VERTEX,{"derivedFrom":[sQuery(id+"F0.wireOp",EDGE,"E9.0"),subQ0]});var subQ5=makeQuery(id+"F0.imprint","INTERSECT",VERTEX,{"derivedFrom":[sQuery(id+"F0.wireOp",EDGE,"E4"),subQ0]});var subQ6=makeQuery(id+"F0.imprint","INTERSECT",VERTEX,{"derivedFrom":[sQuery(id+"F0.wireOp",EDGE,"E8.0"),subQ0]});Q23=makeQuery(id+"F1.opExtrude","CAP_EDGE",EDGE,{"disambiguationData":[OSD([subQ0]),TDD([makeQuery(id+"F0.imprint","IMPRINT",EDGE,{"disambiguationData":[TD([[subQ6,1.0]])],"derivedFrom":subQ0}),makeQuery(id+"F0.imprint","IMPRINT",EDGE,{"disambiguationData":[TD([[subQ5,1.0]])],"derivedFrom":subQ0}),makeQuery(id+"F0.imprint","IMPRINT",EDGE,{"disambiguationData":[TD([[subQ5,-1.0]])],"derivedFrom":subQ0}),makeQuery(id+"F0.imprint","IMPRINT",EDGE,{"disambiguationData":[TD([[subQ4,-1.0]])],"derivedFrom":subQ0}),makeQuery(id+"F0.imprint","IMPRINT",EDGE,{"disambiguationData":[TD([[subQ2,1.0]])],"derivedFrom":subQ0}),makeQuery(id+"F0.imprint","IMPRINT",EDGE,{"disambiguationData":[TD([[subQ2,-1.0]])],"derivedFrom":subQ0}),makeQuery(id+"F0.imprint","IMPRINT",EDGE,{"disambiguationData":[TD([[subQ1,-1.0]])],"derivedFrom":subQ0})])],"isStart":false});}
            var Q24;
            Q24=makeQuery(id+"F1.opExtrude","CAP_EDGE",EDGE,{"disambiguationData":[OSD([sQuery(id+"F0.wireOp",EDGE,"E18")])],"isStart":false});
            var Q25;
            Q25=makeQuery(id+"F1.opExtrude","CAP_EDGE",EDGE,{"disambiguationData":[OSD([sQuery(id+"F0.wireOp",EDGE,"E19")])],"isStart":false});
            var Q26;
            {var subQ0=sQuery(id+"F0.wireOp",EDGE,"E17");var subQ1=makeQuery(id+"F0.imprint","INTERSECT",VERTEX,{"derivedFrom":[sQuery(id+"F0.wireOp",EDGE,"E6"),subQ0]});var subQ3=makeQuery(id+"F0.imprint","INTERSECT",VERTEX,{"derivedFrom":[sQuery(id+"F0.wireOp",EDGE,"E11.0"),subQ0]});var subQ4=makeQuery(id+"F0.imprint","INTERSECT",VERTEX,{"derivedFrom":[sQuery(id+"F0.wireOp",EDGE,"E5"),subQ0]});var subQ5=makeQuery(id+"F0.imprint","INTERSECT",VERTEX,{"derivedFrom":[sQuery(id+"F0.wireOp",EDGE,"E10.0"),subQ0]});var subQ6=makeQuery(id+"F0.imprint","INTERSECT",VERTEX,{"derivedFrom":[sQuery(id+"F0.wireOp",EDGE,"E13.0"),subQ0]});Q26=makeQuery(id+"F1.opExtrude","CAP_EDGE",EDGE,{"disambiguationData":[OSD([subQ0]),TDD([makeQuery(id+"F0.imprint","IMPRINT",EDGE,{"disambiguationData":[TD([[subQ1,-1.0]])],"derivedFrom":subQ0}),makeQuery(id+"F0.imprint","IMPRINT",EDGE,{"disambiguationData":[TD([[subQ6,-1.0]])],"derivedFrom":subQ0}),makeQuery(id+"F0.imprint","IMPRINT",EDGE,{"disambiguationData":[TD([[subQ5,1.0]])],"derivedFrom":subQ0}),makeQuery(id+"F0.imprint","IMPRINT",EDGE,{"disambiguationData":[TD([[subQ4,1.0]])],"derivedFrom":subQ0}),makeQuery(id+"F0.imprint","IMPRINT",EDGE,{"disambiguationData":[TD([[subQ4,-1.0]])],"derivedFrom":subQ0}),makeQuery(id+"F0.imprint","IMPRINT",EDGE,{"disambiguationData":[TD([[subQ3,-1.0]])],"derivedFrom":subQ0}),makeQuery(id+"F0.imprint","IMPRINT",EDGE,{"disambiguationData":[TD([[subQ1,1.0]])],"derivedFrom":subQ0})])],"isStart":false});}
            var Q27;
            {var subQ0=sQuery(id+"F0.wireOp",EDGE,"E16");var subQ1=makeQuery(id+"F0.imprint","INTERSECT",VERTEX,{"derivedFrom":[sQuery(id+"F0.wireOp",EDGE,"E6"),subQ0]});var subQ3=makeQuery(id+"F0.imprint","INTERSECT",VERTEX,{"derivedFrom":[sQuery(id+"F0.wireOp",EDGE,"E11.0"),subQ0]});var subQ4=makeQuery(id+"F0.imprint","INTERSECT",VERTEX,{"derivedFrom":[sQuery(id+"F0.wireOp",EDGE,"E5"),subQ0]});Q27=makeQuery(id+"F1.opExtrude","CAP_EDGE",EDGE,{"disambiguationData":[OSD([subQ0]),TDD([makeQuery(id+"F0.imprint","IMPRINT",EDGE,{"disambiguationData":[TD([[subQ1,-1.0]])],"derivedFrom":subQ0}),makeQuery(id+"F0.imprint","IMPRINT",EDGE,{"disambiguationData":[TD([[makeQuery(id+"F0.imprint","INTERSECT",VERTEX,{"derivedFrom":[subQ0,sQuery(id+"F0.wireOp",EDGE,"E26.0")]}),1.0]])],"derivedFrom":subQ0}),makeQuery(id+"F0.imprint","IMPRINT",EDGE,{"disambiguationData":[TD([[makeQuery(id+"F0.imprint","INTERSECT",VERTEX,{"derivedFrom":[subQ0,sQuery(id+"F0.wireOp",EDGE,"E27.0")]}),-1.0]])],"derivedFrom":subQ0}),makeQuery(id+"F0.imprint","IMPRINT",EDGE,{"disambiguationData":[TD([[subQ4,1.0]])],"derivedFrom":subQ0}),makeQuery(id+"F0.imprint","IMPRINT",EDGE,{"disambiguationData":[TD([[subQ4,-1.0]])],"derivedFrom":subQ0}),makeQuery(id+"F0.imprint","IMPRINT",EDGE,{"disambiguationData":[TD([[subQ3,-1.0]])],"derivedFrom":subQ0}),makeQuery(id+"F0.imprint","IMPRINT",EDGE,{"disambiguationData":[TD([[subQ1,1.0]])],"derivedFrom":subQ0})])],"isStart":false});}
            var Q28;
            {var subQ0=sQuery(id+"F0.wireOp",EDGE,"E3");Q28=makeQuery(id+"F1.opExtrude","CAP_EDGE",EDGE,{"disambiguationData":[OSD([subQ0]),TDD([makeQuery(id+"F0.imprint","IMPRINT",EDGE,{"disambiguationData":[TD([[makeQuery(id+"F0.imprint","INTERSECT",VERTEX,{"derivedFrom":[subQ0,sQuery(id+"F0.wireOp",EDGE,"E11.0")]}),-1.0]])],"derivedFrom":subQ0})])],"isStart":false});}
            var Q29;
            {var subQ0=sQuery(id+"F0.wireOp",EDGE,"E2");Q29=makeQuery(id+"F1.opExtrude","CAP_EDGE",EDGE,{"disambiguationData":[OSD([subQ0]),TDD([makeQuery(id+"F0.imprint","IMPRINT",EDGE,{"disambiguationData":[TD([[makeQuery(id+"F0.imprint","INTERSECT",VERTEX,{"derivedFrom":[subQ0,sQuery(id+"F0.wireOp",EDGE,"E11.0")]}),-1.0]])],"derivedFrom":subQ0})])],"isStart":false});}
            var Q30;
            {var subQ0=sQuery(id+"F0.wireOp",EDGE,"E3");Q30=makeQuery(id+"F1.opExtrude","CAP_EDGE",EDGE,{"disambiguationData":[OSD([subQ0]),TDD([makeQuery(id+"F0.imprint","IMPRINT",EDGE,{"disambiguationData":[TD([[makeQuery(id+"F0.imprint","INTERSECT",VERTEX,{"derivedFrom":[subQ0,sQuery(id+"F0.wireOp",EDGE,"E15.0")]}),-1.0]])],"derivedFrom":subQ0})])],"isStart":false});}
            var Q31;
            {var subQ0=sQuery(id+"F0.wireOp",EDGE,"E2");Q31=makeQuery(id+"F1.opExtrude","CAP_EDGE",EDGE,{"disambiguationData":[OSD([subQ0]),TDD([makeQuery(id+"F0.imprint","IMPRINT",EDGE,{"disambiguationData":[TD([[makeQuery(id+"F0.imprint","INTERSECT",VERTEX,{"derivedFrom":[subQ0,sQuery(id+"F0.wireOp",EDGE,"E15.0")]}),-1.0]])],"derivedFrom":subQ0})])],"isStart":false});}
            fillet(context, id + "F3", {"entities" : qUnion([Q0, Q1, Q2, Q3, Q4, Q5, Q6, Q7, Q8, Q9, Q10, Q11, Q12, Q13, Q14, Q15, Q16, Q17, Q18, Q19, Q20, Q21, Q22, Q23, Q24, Q25, Q26, Q27, Q28, Q29, Q30, Q31]), "radius" : 0.5 * mm, "tangentPropagation" : true, "allowEdgeOverflow" : false});
        }
        {
            var Q0;
            Q0=qCreatedBy(makeId("Top.planeOp"),FACE);
            var sketch = newSketch(context, id + "F4", { "sketchPlane" : qUnion([Q0])});
            skLineSegment(sketch, "E28.bottom", {"start": v(-63.5, 63.5) * mm, "end": v(63.5, 63.5) * mm});
            skLineSegment(sketch, "E28.top", {"start": v(-63.5, -63.5) * mm, "end": v(63.5, -63.5) * mm});
            skLineSegment(sketch, "E28.left", {"start": v(-63.5, 63.5) * mm, "end": v(-63.5, -63.5) * mm});
            skLineSegment(sketch, "E28.right", {"start": v(63.5, 63.5) * mm, "end": v(63.5, -63.5) * mm});
            skPoint(sketch, "E28.middle", {"position": v(0, 0) * mm});
            skSolve(sketch);
        }
        {
            var Q0;
            Q0=makeQuery(id+"F4.imprint","IMPRINT",FACE,{"disambiguationData":[TD([[makeQuery(id+"F4.imprint","IMPRINT",EDGE,{"derivedFrom":sQuery(id+"F4.wireOp",EDGE,"E28.bottom")}),-1.0]])]});
            extrude(context, id + "F5", {"entities" : qUnion([Q0]), "depth" : 2.5 * mm});
        }
    });
